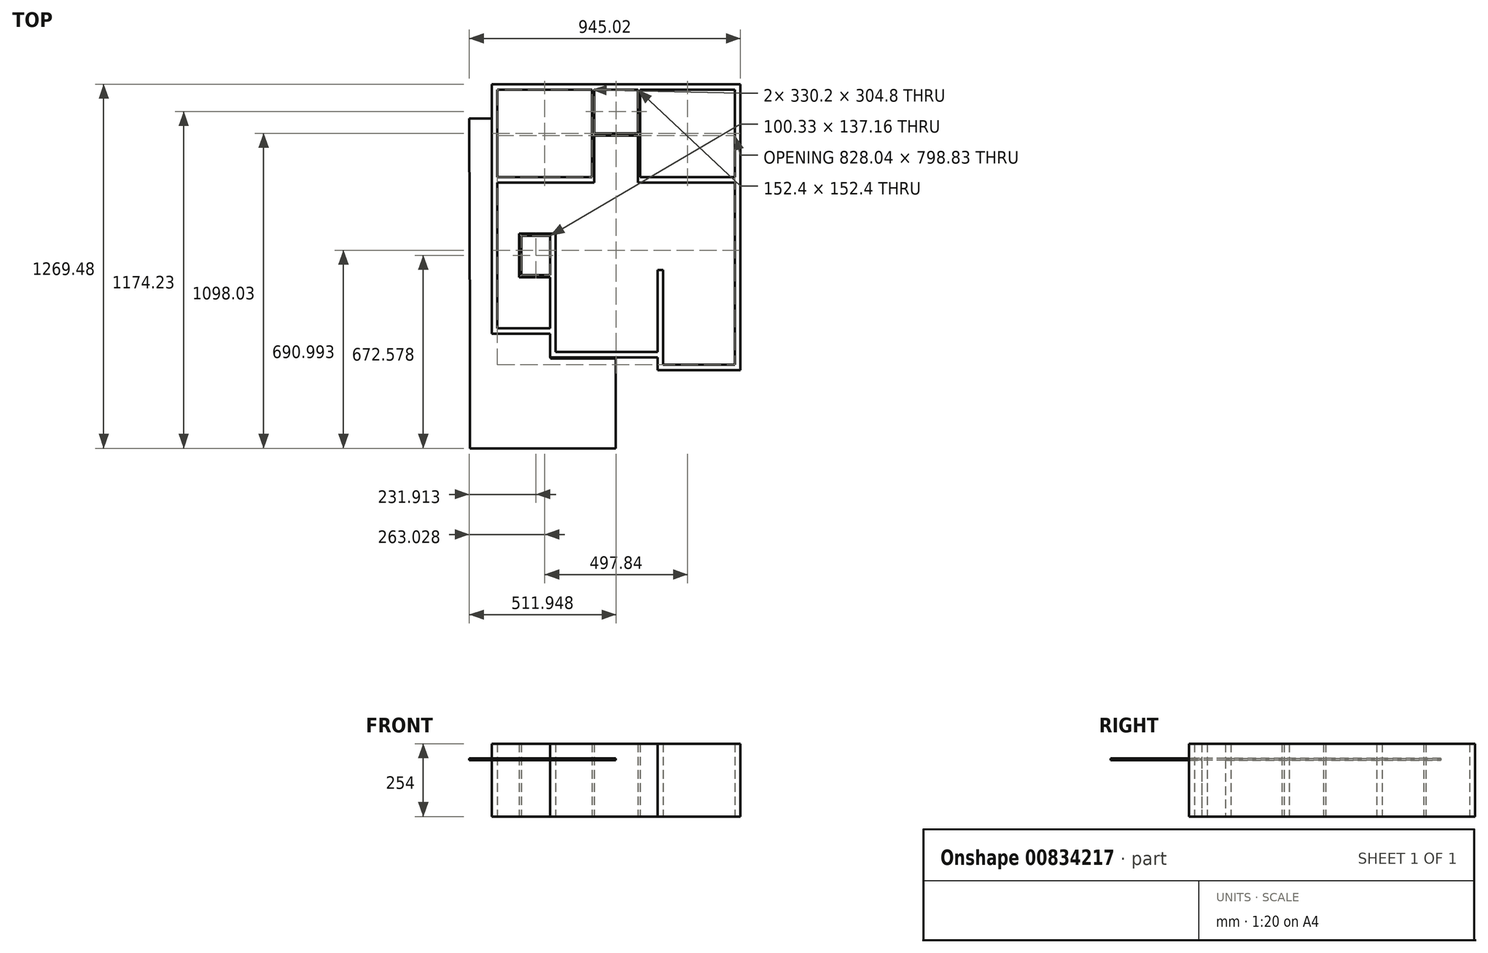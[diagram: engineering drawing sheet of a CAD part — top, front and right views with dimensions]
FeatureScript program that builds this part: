
annotation { "Feature Type Name" : "Feature", "Feature Type Description" : "" }
export const myFeature = defineFeature(function(context is Context, id is Id, definition is map)
    precondition{}
    {
        {
            var Q0;
            Q0=qCreatedBy(makeId("Top.planeOp"),FACE);
            var sketch = newSketch(context, id + "F0", { "sketchPlane" : qUnion([Q0])});
            skLineSegment(sketch, "E0.bottom", {"start": v(-386.54, 364.79) * mm, "end": v(-56.34, 364.79) * mm});
            skLineSegment(sketch, "E0.top", {"start": v(-386.54, 59.99) * mm, "end": v(-56.34, 59.99) * mm});
            skLineSegment(sketch, "E0.left", {"start": v(-386.54, 364.79) * mm, "end": v(-386.54, 59.99) * mm});
            skLineSegment(sketch, "E0.right", {"start": v(-56.34, 364.79) * mm, "end": v(-56.34, 59.99) * mm});
            skLineSegment(sketch, "E1.bottom", {"start": v(-48.72, 364.79) * mm, "end": v(103.68, 364.79) * mm});
            skLineSegment(sketch, "E1.top", {"start": v(-48.72, 212.39) * mm, "end": v(103.68, 212.39) * mm});
            skLineSegment(sketch, "E1.left", {"start": v(-48.72, 364.79) * mm, "end": v(-48.72, 212.39) * mm});
            skLineSegment(sketch, "E1.right", {"start": v(103.68, 364.79) * mm, "end": v(103.68, 212.39) * mm});
            skLineSegment(sketch, "E2.bottom", {"start": v(111.3, 364.79) * mm, "end": v(441.5, 364.79) * mm});
            skLineSegment(sketch, "E2.top", {"start": v(111.3, 59.99) * mm, "end": v(441.5, 59.99) * mm});
            skLineSegment(sketch, "E2.left", {"start": v(111.3, 364.79) * mm, "end": v(111.3, 59.99) * mm});
            skLineSegment(sketch, "E2.right", {"start": v(441.5, 364.79) * mm, "end": v(441.5, 59.99) * mm});
            skPoint(sketch, "E3", {"position": v(-405.6, 383.84) * mm});
            skLineSegment(sketch, "E4", {"start": v(-405.6, 383.84) * mm, "end": v(460.55, 383.84) * mm});
            skLineSegment(sketch, "E5", {"start": v(103.68, 364.79) * mm, "end": v(111.3, 364.79) * mm});
            skLineSegment(sketch, "E6", {"start": v(-405.6, 383.84) * mm, "end": v(-405.6, 40.94) * mm});
            skPoint(sketch, "E7", {"position": v(-386.54, 40.94) * mm});
            skLineSegment(sketch, "E8", {"start": v(-386.54, 40.94) * mm, "end": v(-48.72, 40.94) * mm});
            skLineSegment(sketch, "E9", {"start": v(-48.72, 40.94) * mm, "end": v(-48.72, 204.77) * mm});
            skLineSegment(sketch, "E10", {"start": v(-48.72, 204.77) * mm, "end": v(103.68, 204.77) * mm});
            skLineSegment(sketch, "E11", {"start": v(103.68, 204.77) * mm, "end": v(103.68, 40.94) * mm});
            skLineSegment(sketch, "E12", {"start": v(103.68, 40.94) * mm, "end": v(441.5, 40.94) * mm});
            skLineSegment(sketch, "E13", {"start": v(-386.54, 40.94) * mm, "end": v(-386.54, -467.06) * mm});
            skPoint(sketch, "E14", {"position": v(-310.34, -136.86) * mm});
            skLineSegment(sketch, "E15", {"start": v(-310.34, -136.86) * mm, "end": v(-183.34, -136.86) * mm});
            skLineSegment(sketch, "E16", {"start": v(-310.34, -289.26) * mm, "end": v(-310.34, -136.86) * mm});
            skLineSegment(sketch, "E17", {"start": v(-386.54, -467.06) * mm, "end": v(-202.4, -467.06) * mm});
            skLineSegment(sketch, "E18", {"start": v(-405.6, 40.94) * mm, "end": v(-405.6, -486.11) * mm});
            skLineSegment(sketch, "E19", {"start": v(-183.34, -486.11) * mm, "end": v(-183.34, -136.86) * mm});
            skLineSegment(sketch, "E20", {"start": v(-202.4, -467.06) * mm, "end": v(-202.4, -144.48) * mm});
            skLineSegment(sketch, "E21", {"start": v(-202.4, -144.48) * mm, "end": v(-302.72, -144.48) * mm});
            skLineSegment(sketch, "E22", {"start": v(-302.72, -144.48) * mm, "end": v(-302.72, -281.64) * mm});
            skLineSegment(sketch, "E23", {"start": v(-302.72, -281.64) * mm, "end": v(-202.4, -281.64) * mm});
            skPoint(sketch, "E24", {"position": v(-183.34, -263.86) * mm});
            skLineSegment(sketch, "E25", {"start": v(172.26, -263.86) * mm, "end": v(191.3, -263.86) * mm});
            skLineSegment(sketch, "E26", {"start": v(441.5, 40.94) * mm, "end": v(441.5, -263.86) * mm});
            skLineSegment(sketch, "E27", {"start": v(460.55, 383.84) * mm, "end": v(460.55, -282.91) * mm});
            skLineSegment(sketch, "E28.bottom", {"start": v(441.5, 40.94) * mm, "end": v(289.1, 40.94) * mm});
            skLineSegment(sketch, "E28.left", {"start": v(441.5, 40.94) * mm, "end": v(441.5, -86.06) * mm});
            skLineSegment(sketch, "E29.bottom", {"start": v(441.5, 40.94) * mm, "end": v(281.48, 40.94) * mm});
            skLineSegment(sketch, "E29.left", {"start": v(441.5, 40.94) * mm, "end": v(441.5, -93.68) * mm});
            skLineSegment(sketch, "E30", {"start": v(-310.34, -289.26) * mm, "end": v(-202.4, -289.26) * mm});
            skLineSegment(sketch, "E31", {"start": v(-183.34, -486.11) * mm, "end": v(-183.34, -549.61) * mm});
            skPoint(sketch, "E32", {"position": v(-183.34, -486.11) * mm});
            skPoint(sketch, "E33", {"position": v(-183.34, -549.61) * mm});
            skLineSegment(sketch, "E34", {"start": v(-183.34, -549.61) * mm, "end": v(172.26, -549.61) * mm});
            skLineSegment(sketch, "E35", {"start": v(172.26, -549.61) * mm, "end": v(172.26, -263.86) * mm});
            skLineSegment(sketch, "E36", {"start": v(191.3, -263.86) * mm, "end": v(191.3, -594.06) * mm});
            skLineSegment(sketch, "E37", {"start": v(-405.6, -486.11) * mm, "end": v(-202.4, -486.11) * mm});
            skLineSegment(sketch, "E38", {"start": v(-202.4, -486.11) * mm, "end": v(-202.4, -568.66) * mm});
            skLineSegment(sketch, "E39", {"start": v(-202.4, -568.66) * mm, "end": v(172.26, -568.66) * mm});
            skLineSegment(sketch, "E40", {"start": v(191.3, -594.06) * mm, "end": v(441.5, -594.06) * mm});
            skLineSegment(sketch, "E41", {"start": v(441.5, -263.86) * mm, "end": v(441.5, -594.06) * mm});
            skLineSegment(sketch, "E42", {"start": v(172.26, -568.66) * mm, "end": v(172.26, -613.11) * mm});
            skLineSegment(sketch, "E43", {"start": v(172.26, -613.11) * mm, "end": v(460.55, -613.11) * mm});
            skLineSegment(sketch, "E44", {"start": v(460.55, -282.91) * mm, "end": v(460.55, -613.11) * mm});
            skLineSegment(sketch, "E45", {"start": v(-405.6, -486.11) * mm, "end": v(-481.8, -486.11) * mm});
            skLineSegment(sketch, "E46", {"start": v(-481.8, -486.11) * mm, "end": v(-481.8, -886.16) * mm});
            skLineSegment(sketch, "E47", {"start": v(-481.8, -886.16) * mm, "end": v(26.2, -886.16) * mm});
            skLineSegment(sketch, "E48", {"start": v(26.2, -886.16) * mm, "end": v(26.2, -568.66) * mm});
            skSolve(sketch);
        }
        {
            var Q0;
            Q0=makeQuery(id+"F0.imprint","IMPRINT",FACE,{"disambiguationData":[TD([[makeQuery(id+"F0.imprint","IMPRINT",EDGE,{"derivedFrom":sQuery(id+"F0.wireOp",EDGE,"E0.bottom")}),1.0]])]});
            extrude(context, id + "F1", {"entities" : qUnion([Q0]), "depth" : 254 * mm, "offsetDistance" : 25.4 * mm});
        }
        {
            var Q0;
            Q0=makeQuery(id+"F0.imprint","IMPRINT",FACE,{"disambiguationData":[TD([[makeQuery(id+"F0.imprint","IMPRINT",EDGE,{"derivedFrom":sQuery(id+"F0.wireOp",EDGE,"E37")}),-1.0]])]});
            cPlane(context, id + "F2", {"entities" : qUnion([Q0]), "cplaneType" : CPlaneType.OFFSET, "offset" : 203.2 * mm, "width" : 152.4 * mm, "height" : 152.4 * mm});
        }
        {
            var Q0;
            Q0=qCreatedBy(id+"F2.planeOp",FACE);
            var sketch = newSketch(context, id + "F3", { "sketchPlane" : qUnion([Q0])});
            skLineSegment(sketch, "E49", {"start": v(-202.2, -484.55) * mm, "end": v(-481.6, -484.55) * mm});
            skLineSegment(sketch, "E50", {"start": v(-481.6, -484.55) * mm, "end": v(-481.6, -885.64) * mm});
            skLineSegment(sketch, "E51", {"start": v(-481.6, -885.64) * mm, "end": v(26.4, -885.64) * mm});
            skLineSegment(sketch, "E52", {"start": v(26.4, -885.64) * mm, "end": v(26.4, -572.29) * mm});
            skLineSegment(sketch, "E53", {"start": v(26.4, -572.29) * mm, "end": v(-202.2, -572.29) * mm});
            skLineSegment(sketch, "E54", {"start": v(-202.2, -572.29) * mm, "end": v(-202.2, -484.55) * mm});
            skSolve(sketch);
        }
        {
            var Q0;
            Q0=makeQuery(id+"F3.imprint","IMPRINT",FACE,{"disambiguationData":[TD([[makeQuery(id+"F3.imprint","IMPRINT",EDGE,{"derivedFrom":sQuery(id+"F3.wireOp",EDGE,"E49")}),1.0]])]});
            extrude(context, id + "F4", {"entities" : qUnion([Q0]), "operationType" : NewBodyOperationType.ADD, "oppositeDirection" : true, "depth" : 6.35 * mm, "offsetDistance" : 25.4 * mm});
        }
        {
            var Q0;
            Q0=makeQuery(id+"F4.opExtrude","CAP_FACE",FACE,{"disambiguationData":[OSD([sQuery(id+"F3.wireOp",EDGE,"E49"),sQuery(id+"F3.wireOp",EDGE,"E50"),sQuery(id+"F3.wireOp",EDGE,"E51"),sQuery(id+"F3.wireOp",EDGE,"E52"),sQuery(id+"F3.wireOp",EDGE,"E53"),sQuery(id+"F3.wireOp",EDGE,"E54")])],"isStart":true});
            var sketch = newSketch(context, id + "F5", { "sketchPlane" : qUnion([Q0])});
            skLineSegment(sketch, "E55", {"start": v(-481.6, -484.55) * mm, "end": v(-481.6, -484.55) * mm});
            skLineSegment(sketch, "E56", {"start": v(-481.6, -484.55) * mm, "end": v(-484.47, 264.83) * mm});
            skLineSegment(sketch, "E57", {"start": v(-484.47, 264.83) * mm, "end": v(-401.74, 264.83) * mm});
            skLineSegment(sketch, "E58", {"start": v(-401.74, 264.83) * mm, "end": v(-405.6, -486.11) * mm});
            skSolve(sketch);
        }
        {
            var Q0;
            Q0=makeQuery(id+"F5.imprint","IMPRINT",FACE,{"disambiguationData":[TD([[makeQuery(id+"F5.imprint","IMPRINT",EDGE,{"derivedFrom":sQuery(id+"F5.wireOp",EDGE,"E56")}),-1.0]])]});
            extrude(context, id + "F6", {"entities" : qUnion([Q0]), "operationType" : NewBodyOperationType.ADD, "oppositeDirection" : true, "depth" : 6.35 * mm, "offsetDistance" : 25.4 * mm});
        }
    });
